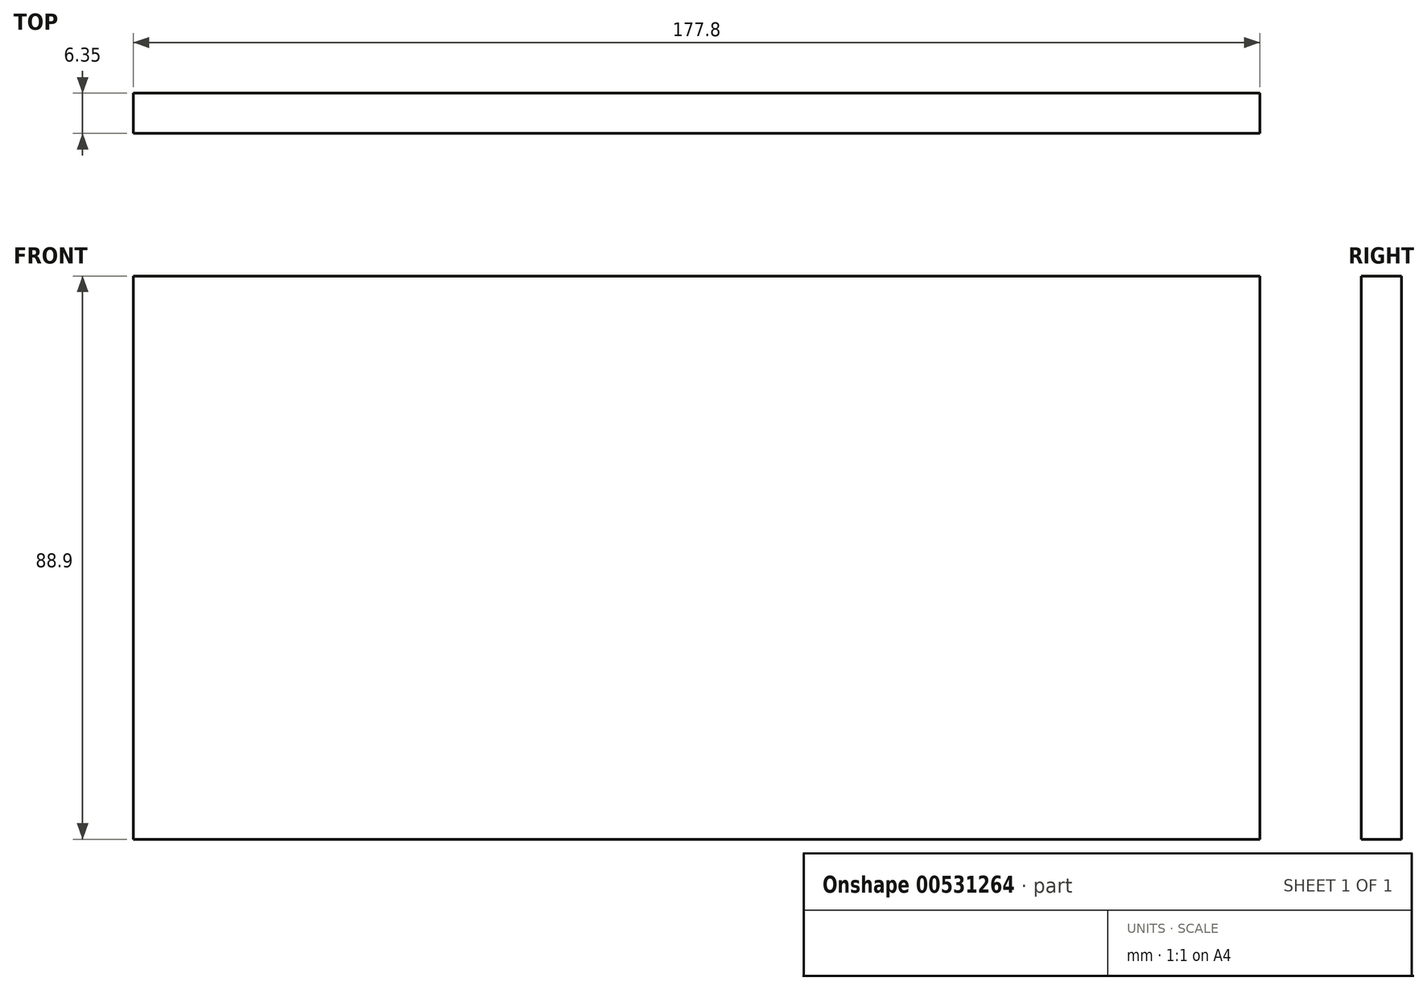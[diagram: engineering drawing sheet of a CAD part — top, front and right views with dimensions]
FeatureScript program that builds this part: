
annotation { "Feature Type Name" : "Feature", "Feature Type Description" : "" }
export const myFeature = defineFeature(function(context is Context, id is Id, definition is map)
    precondition{}
    {
        {
            var Q0;
            Q0=qCreatedBy(makeId("Front.planeOp"),FACE);
            var sketch = newSketch(context, id + "F0", { "sketchPlane" : qUnion([Q0])});
            skLineSegment(sketch, "E0.bottom", {"start": v(-85.84, 41.6) * mm, "end": v(91.96, 41.6) * mm});
            skLineSegment(sketch, "E0.top", {"start": v(-85.84, -47.3) * mm, "end": v(91.96, -47.3) * mm});
            skLineSegment(sketch, "E0.left", {"start": v(-85.84, 41.6) * mm, "end": v(-85.84, -47.3) * mm});
            skLineSegment(sketch, "E0.right", {"start": v(91.96, 41.6) * mm, "end": v(91.96, -47.3) * mm});
            skSolve(sketch);
        }
        {
            var Q0;
            Q0=makeQuery(id+"F0.imprint","IMPRINT",FACE,{"disambiguationData":[TD([[makeQuery(id+"F0.imprint","IMPRINT",EDGE,{"derivedFrom":sQuery(id+"F0.wireOp",EDGE,"E0.bottom")}),-1.0]])]});
            extrude(context, id + "F1", {"entities" : qUnion([Q0]), "depth" : 6.35 * mm, "offsetDistance" : 25.4 * mm});
        }
    });
